# Revit family: 51306XXX_new
name_source: partatom
category: Furniture
revit_build: Autodesk Revit 2018 (Build: 20170223_1515(x64)
units: mm (PartAtom-declared; Revit-internal decimal feet)

## family parameters
Always vertical = No
Cut with Voids When Loaded = No
OmniClass Number = 23.40.20.00
OmniClass Title = General Furniture and Specialties
Room Calculation Point = No
Shared = No
Work Plane-Based = No

## types (1)
- Default - please load Revit Family Type Catalog
    Always visible = Yes
    BIMobject category = Sanitary Accessories
    Design country = Germany
    EAN code = 4059625077689
    Edition number = 1
    GTIN code = https://4059625077689
    IFC Classification = Sanitary Terminal
    Installation instructions = https://www.axor-design.com
    Manufacturer country = Germany
    Manufacturer name = AXOR
    Material 1 = AXOR - AXOR One - 000 Chrome
    Material main = Chrome
    Product Guid = 0f9011bd-74fc-422e-87a5-cc59faeb5313
    Product SKU = 51306XXX
    Product data url = https://www.bimobject.com
    Product family = AXOR
    Product group = Siphons/Angle valves
    Product name = 51306XXX AXOR Cover
    Product url = https://www.axor-design.com
    QR code = https://www.bimobject.com
    Technical description = https://www.axor-design.com
